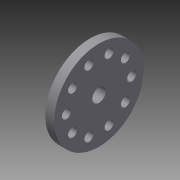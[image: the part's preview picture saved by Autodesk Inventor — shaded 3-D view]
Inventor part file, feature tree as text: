
AUTODESK INVENTOR PART (.ipt)
format: ipt  version: 2015 (Build 190159000, 159)  size: 119,808 bytes
history: native  units: in
note: dims shown in document units (in); Inventor stores cm internally (conversion verified against a paired STEP export)
features: sketch x2, revolve x1, hole x1
ambient origin geometry x8: Origin, YZ Plane, XZ Plane, XY Plane, X Axis, Y Axis, Z Axis, Center Point
bodies: Body1 (feature_tree)
feature tree (4):
  revolve  "Revolution2"  [1 undecoded]
  hole  "Hole2"  [1 undecoded]
  sketch  "Sketch1"  dims[d0=1.0in d1=0.375in]
  sketch  "Sketch7"  dims[d2=0.625in d3=0.5in d4=1.5in d6=90.0deg d14=3.65in d15=3.937in d17=360.0deg d19=0.5in d20=0.75in d21=0.375in d22=0.25in d23=0.5635in d24=1.0in d25=0.8108in]
note: 2 required parameter values undecoded (feature->parameter linkage not recoverable at this tier; creation-order binding heuristic only, values carry confidence <= 0.55)